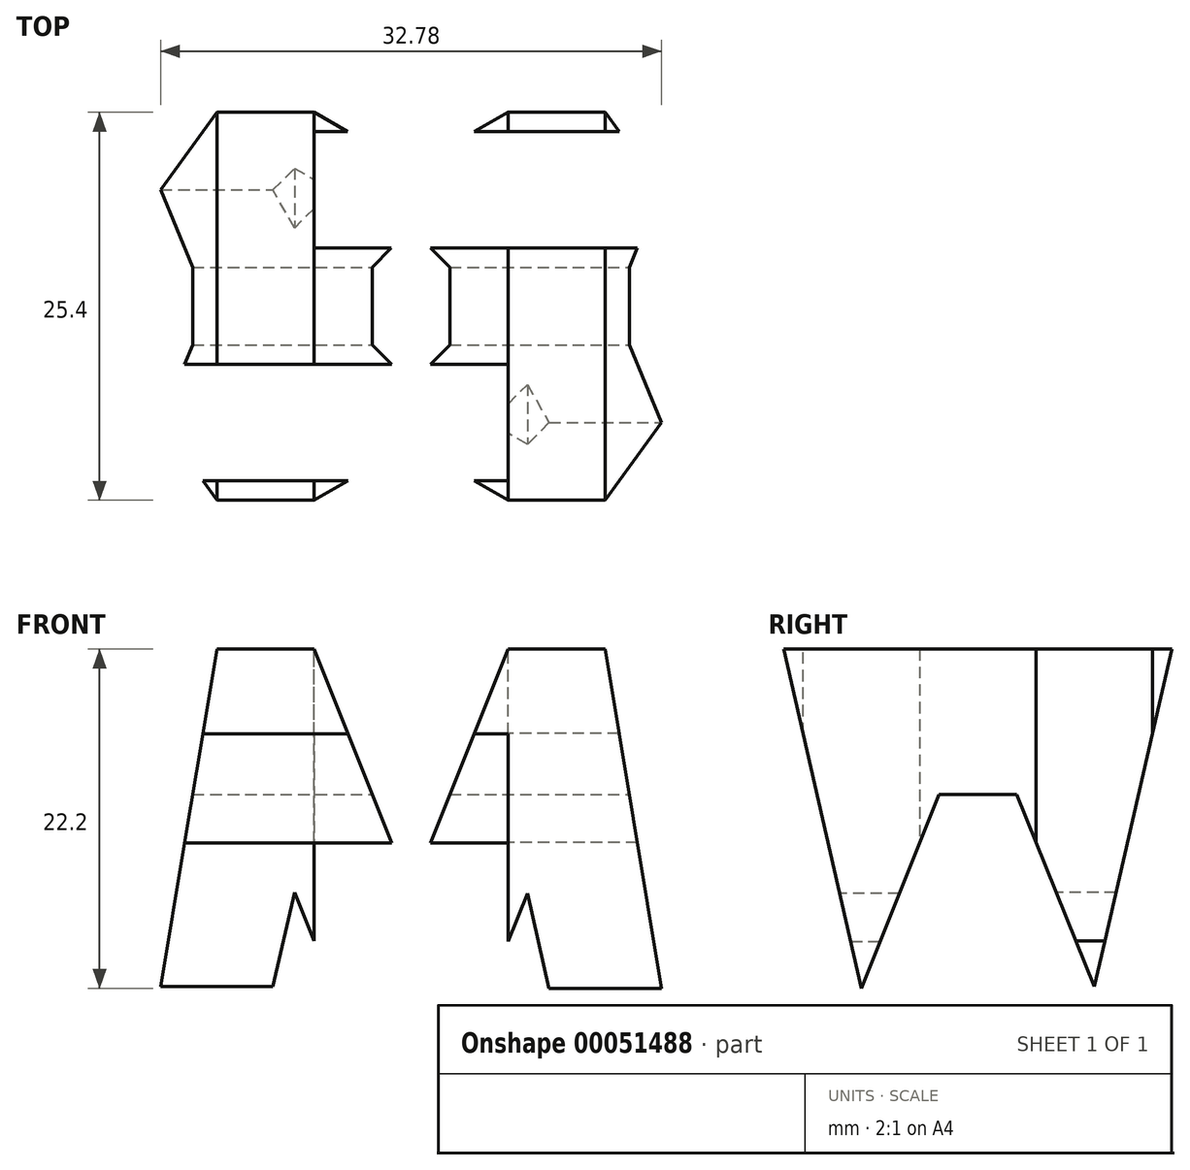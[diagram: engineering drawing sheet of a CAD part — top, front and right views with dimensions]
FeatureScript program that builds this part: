
annotation { "Feature Type Name" : "Feature", "Feature Type Description" : "" }
export const myFeature = defineFeature(function(context is Context, id is Id, definition is map)
    precondition{}
    {
        {
            var Q0;
            Q0=qCreatedBy(makeId("Front.planeOp"),FACE);
            var sketch = newSketch(context, id + "F0", { "sketchPlane" : qUnion([Q0])});
            skLineSegment(sketch, "E0", {"start": v(0, 0) * mm, "end": v(-38.1, 0) * mm});
            skLineSegment(sketch, "E1", {"start": v(-38.1, 0) * mm, "end": v(-38.1, 38.1) * mm});
            skLineSegment(sketch, "E2", {"start": v(-38.1, 38.1) * mm, "end": v(0, 38.1) * mm});
            skLineSegment(sketch, "E3", {"start": v(0, 38.1) * mm, "end": v(0, 0) * mm});
            skSolve(sketch);
        }
        {
            var Q0;
            Q0=makeQuery(id+"F0.imprint","IMPRINT",FACE,{"disambiguationData":[TD([[makeQuery(id+"F0.imprint","IMPRINT",EDGE,{"derivedFrom":sQuery(id+"F0.wireOp",EDGE,"E0")}),-1.0]])]});
            extrude(context, id + "F1", {"entities" : qUnion([Q0]), "depth" : 38.1 * mm});
        }
        {
            var Q0;
            Q0=qCreatedBy(makeId("Front.planeOp"),FACE);
            cPlane(context, id + "F2", {"entities" : qUnion([Q0]), "cplaneType" : CPlaneType.OFFSET, "offset" : 38.1 * mm, "width" : 152.4 * mm, "height" : 152.4 * mm});
        }
        {
            var Q0;
            Q0=qCreatedBy(makeId("Right.planeOp"),FACE);
            cPlane(context, id + "F3", {"entities" : qUnion([Q0]), "cplaneType" : CPlaneType.OFFSET, "offset" : 38.1 * mm, "width" : 152.4 * mm, "height" : 152.4 * mm});
        }
        {
            var Q0;
            Q0=qCreatedBy(makeId("Top.planeOp"),FACE);
            cPlane(context, id + "F4", {"entities" : qUnion([Q0]), "cplaneType" : CPlaneType.OFFSET, "offset" : 38.1 * mm, "width" : 152.4 * mm, "height" : 152.4 * mm});
        }
        {
            var Q0;
            Q0=qCreatedBy(id+"F3.planeOp",FACE);
            var sketch = newSketch(context, id + "F5", { "sketchPlane" : qUnion([Q0])});
            skLineSegment(sketch, "E4", {"start": v(0, 0) * mm, "end": v(0, 38.1) * mm});
            skLineSegment(sketch, "E5", {"start": v(0, 38.1) * mm, "end": v(-38.1, 38.1) * mm});
            skLineSegment(sketch, "E6", {"start": v(-38.1, 38.1) * mm, "end": v(-38.1, 0) * mm});
            skLineSegment(sketch, "E7", {"start": v(-38.1, 0) * mm, "end": v(0, 0) * mm});
            skLineSegment(sketch, "E8", {"start": v(-38.1, 38.1) * mm, "end": v(-31.75, 0) * mm});
            skLineSegment(sketch, "E9", {"start": v(-25.4, 0) * mm, "end": v(-19.05, 15.88) * mm});
            skLineSegment(sketch, "E10", {"start": v(-19.05, 15.88) * mm, "end": v(-12.7, 0) * mm});
            skLineSegment(sketch, "E11", {"start": v(-6.35, 0) * mm, "end": v(0, 38.1) * mm});
            skLineSegment(sketch, "E12", {"start": v(-6.35, 38.1) * mm, "end": v(-11.43, 16.01) * mm});
            skLineSegment(sketch, "E13", {"start": v(-11.43, 16.01) * mm, "end": v(-16.51, 28.58) * mm});
            skLineSegment(sketch, "E14", {"start": v(-16.51, 28.58) * mm, "end": v(-21.6, 28.58) * mm});
            skLineSegment(sketch, "E15", {"start": v(-21.59, 28.58) * mm, "end": v(-26.67, 15.9) * mm});
            skLineSegment(sketch, "E16", {"start": v(-26.67, 15.9) * mm, "end": v(-31.75, 38.1) * mm});
            skLineSegment(sketch, "E17", {"start": v(-38.1, 38.1) * mm, "end": v(-31.75, 38.1) * mm});
            skLineSegment(sketch, "E18", {"start": v(-6.35, 38.1) * mm, "end": v(0, 38.1) * mm});
            skLineSegment(sketch, "E19", {"start": v(-12.7, 0) * mm, "end": v(-6.35, 0) * mm});
            skLineSegment(sketch, "E20", {"start": v(-25.4, 0) * mm, "end": v(-31.75, 0) * mm});
            skLineSegment(sketch, "E21", {"start": v(-31.75, 0) * mm, "end": v(-25.4, 0) * mm});
            skLineSegment(sketch, "E22", {"start": v(-25.4, 0) * mm, "end": v(-12.7, 0) * mm});
            skLineSegment(sketch, "E23", {"start": v(-38.1, 0) * mm, "end": v(-31.75, 0) * mm});
            skLineSegment(sketch, "E24", {"start": v(-6.35, 0) * mm, "end": v(0, 0) * mm});
            skSolve(sketch);
        }
        {
            var Q0;
            Q0=makeQuery(id+"F5.imprint","IMPRINT",FACE,{"disambiguationData":[TD([[makeQuery(id+"F5.imprint","IMPRINT",EDGE,{"derivedFrom":sQuery(id+"F5.wireOp",EDGE,"E6")}),1.0]])]});
            var Q1;
            Q1=makeQuery(id+"F5.imprint","IMPRINT",FACE,{"disambiguationData":[TD([[makeQuery(id+"F5.imprint","IMPRINT",EDGE,{"derivedFrom":sQuery(id+"F5.wireOp",EDGE,"E5")}),1.0]])]});
            var Q2;
            Q2=makeQuery(id+"F5.imprint","IMPRINT",FACE,{"disambiguationData":[TD([[makeQuery(id+"F5.imprint","IMPRINT",EDGE,{"derivedFrom":sQuery(id+"F5.wireOp",EDGE,"E9")}),-1.0]])]});
            var Q3;
            Q3=makeQuery(id+"F5.imprint","IMPRINT",FACE,{"disambiguationData":[TD([[makeQuery(id+"F5.imprint","IMPRINT",EDGE,{"derivedFrom":sQuery(id+"F5.wireOp",EDGE,"E4")}),1.0]])]});
            extrude(context, id + "F6", {"entities" : qUnion([Q0, Q1, Q2, Q3]), "operationType" : NewBodyOperationType.REMOVE, "oppositeDirection" : true, "depth" : 76.2 * mm});
        }
        {
            var Q0;
            Q0=qCreatedBy(id+"F2.planeOp",FACE);
            var sketch = newSketch(context, id + "F7", { "sketchPlane" : qUnion([Q0])});
            skLineSegment(sketch, "E25", {"start": v(-38.1, 38.1) * mm, "end": v(-38.1, 0) * mm});
            skLineSegment(sketch, "E26", {"start": v(-38.1, 38.1) * mm, "end": v(0, 38.1) * mm});
            skLineSegment(sketch, "E27", {"start": v(0, 38.1) * mm, "end": v(0, 0) * mm});
            skLineSegment(sketch, "E28", {"start": v(0, -0.16) * mm, "end": v(-38.1, 0) * mm});
            skLineSegment(sketch, "E29", {"start": v(-38.1, 0) * mm, "end": v(-31.75, 38.1) * mm});
            skLineSegment(sketch, "E30", {"start": v(-25.4, 38.1) * mm, "end": v(-19.05, 22.23) * mm});
            skLineSegment(sketch, "E31", {"start": v(-19.05, 22.23) * mm, "end": v(-12.7, 38.1) * mm});
            skLineSegment(sketch, "E32", {"start": v(-6.35, 38.1) * mm, "end": v(0, 0) * mm});
            skLineSegment(sketch, "E33", {"start": v(-31.75, -0.03) * mm, "end": v(-26.67, 22.18) * mm});
            skLineSegment(sketch, "E34", {"start": v(-26.67, 22.18) * mm, "end": v(-21.6, 9.52) * mm});
            skLineSegment(sketch, "E35", {"start": v(-21.6, 9.53) * mm, "end": v(-16.51, 9.53) * mm});
            skLineSegment(sketch, "E36", {"start": v(-16.51, 9.52) * mm, "end": v(-11.43, 22.11) * mm});
            skLineSegment(sketch, "E37", {"start": v(-11.43, 22.11) * mm, "end": v(-6.35, -0.13) * mm});
            skSolve(sketch);
        }
        {
            var Q0;
            {var subQ0=sQuery(id+"F7.wireOp",EDGE,"E25");Q0=makeQuery(id+"F7.imprint","IMPRINT",FACE,{"disambiguationData":[TD([[makeQuery(id+"F7.imprint","IMPRINT",EDGE,{"derivedFrom":subQ0}),1.0]])]});}
            var Q1;
            {var subQ0=sQuery(id+"F7.wireOp",EDGE,"E30");Q1=makeQuery(id+"F7.imprint","IMPRINT",FACE,{"disambiguationData":[TD([[makeQuery(id+"F7.imprint","IMPRINT",EDGE,{"derivedFrom":subQ0}),1.0]])]});}
            var Q2;
            {var subQ0=sQuery(id+"F7.wireOp",EDGE,"E27");Q2=makeQuery(id+"F7.imprint","IMPRINT",FACE,{"disambiguationData":[TD([[makeQuery(id+"F7.imprint","IMPRINT",EDGE,{"derivedFrom":subQ0}),-1.0]])]});}
            var Q3;
            {var subQ0=sQuery(id+"F7.wireOp",EDGE,"E33");Q3=makeQuery(id+"F7.imprint","IMPRINT",FACE,{"disambiguationData":[TD([[makeQuery(id+"F7.imprint","IMPRINT",EDGE,{"derivedFrom":subQ0}),-1.0]])]});}
            extrude(context, id + "F8", {"entities" : qUnion([Q0, Q1, Q2, Q3]), "operationType" : NewBodyOperationType.REMOVE, "oppositeDirection" : true, "depth" : 38.1 * mm});
        }
        {
            var Q0;
            Q0=qCreatedBy(id+"F4.planeOp",FACE);
            var sketch = newSketch(context, id + "F9", { "sketchPlane" : qUnion([Q0])});
            skLineSegment(sketch, "E38", {"start": v(0, 0) * mm, "end": v(-38.1, 0) * mm});
            skLineSegment(sketch, "E39", {"start": v(-38.1, 0) * mm, "end": v(-38.1, -38.1) * mm});
            skLineSegment(sketch, "E40", {"start": v(-38.1, -38.1) * mm, "end": v(0, -38.1) * mm});
            skLineSegment(sketch, "E41", {"start": v(0, -38.1) * mm, "end": v(0, 0) * mm});
            skLineSegment(sketch, "E42", {"start": v(0, -7.62) * mm, "end": v(-25.4, -7.62) * mm});
            skLineSegment(sketch, "E43", {"start": v(0, -15.24) * mm, "end": v(-25.4, -15.24) * mm});
            skLineSegment(sketch, "E44", {"start": v(-25.4, -7.62) * mm, "end": v(-25.4, -15.24) * mm});
            skLineSegment(sketch, "E45", {"start": v(-38.1, -22.86) * mm, "end": v(-12.7, -22.86) * mm});
            skLineSegment(sketch, "E46", {"start": v(-12.7, -22.86) * mm, "end": v(-12.7, -30.48) * mm});
            skLineSegment(sketch, "E47", {"start": v(-12.7, -30.48) * mm, "end": v(-38.1, -30.48) * mm});
            skSolve(sketch);
        }
        {
            var Q0;
            {var subQ0=sQuery(id+"F9.wireOp",EDGE,"E42");Q0=makeQuery(id+"F9.imprint","IMPRINT",FACE,{"disambiguationData":[TD([[makeQuery(id+"F9.imprint","IMPRINT",EDGE,{"derivedFrom":subQ0}),1.0]])]});}
            var Q1;
            {var subQ0=sQuery(id+"F9.wireOp",EDGE,"E45");Q1=makeQuery(id+"F9.imprint","IMPRINT",FACE,{"disambiguationData":[TD([[makeQuery(id+"F9.imprint","IMPRINT",EDGE,{"derivedFrom":subQ0}),-1.0]])]});}
            extrude(context, id + "F10", {"entities" : qUnion([Q0, Q1]), "operationType" : NewBodyOperationType.REMOVE, "oppositeDirection" : true, "depth" : 38.1 * mm});
        }
    });
